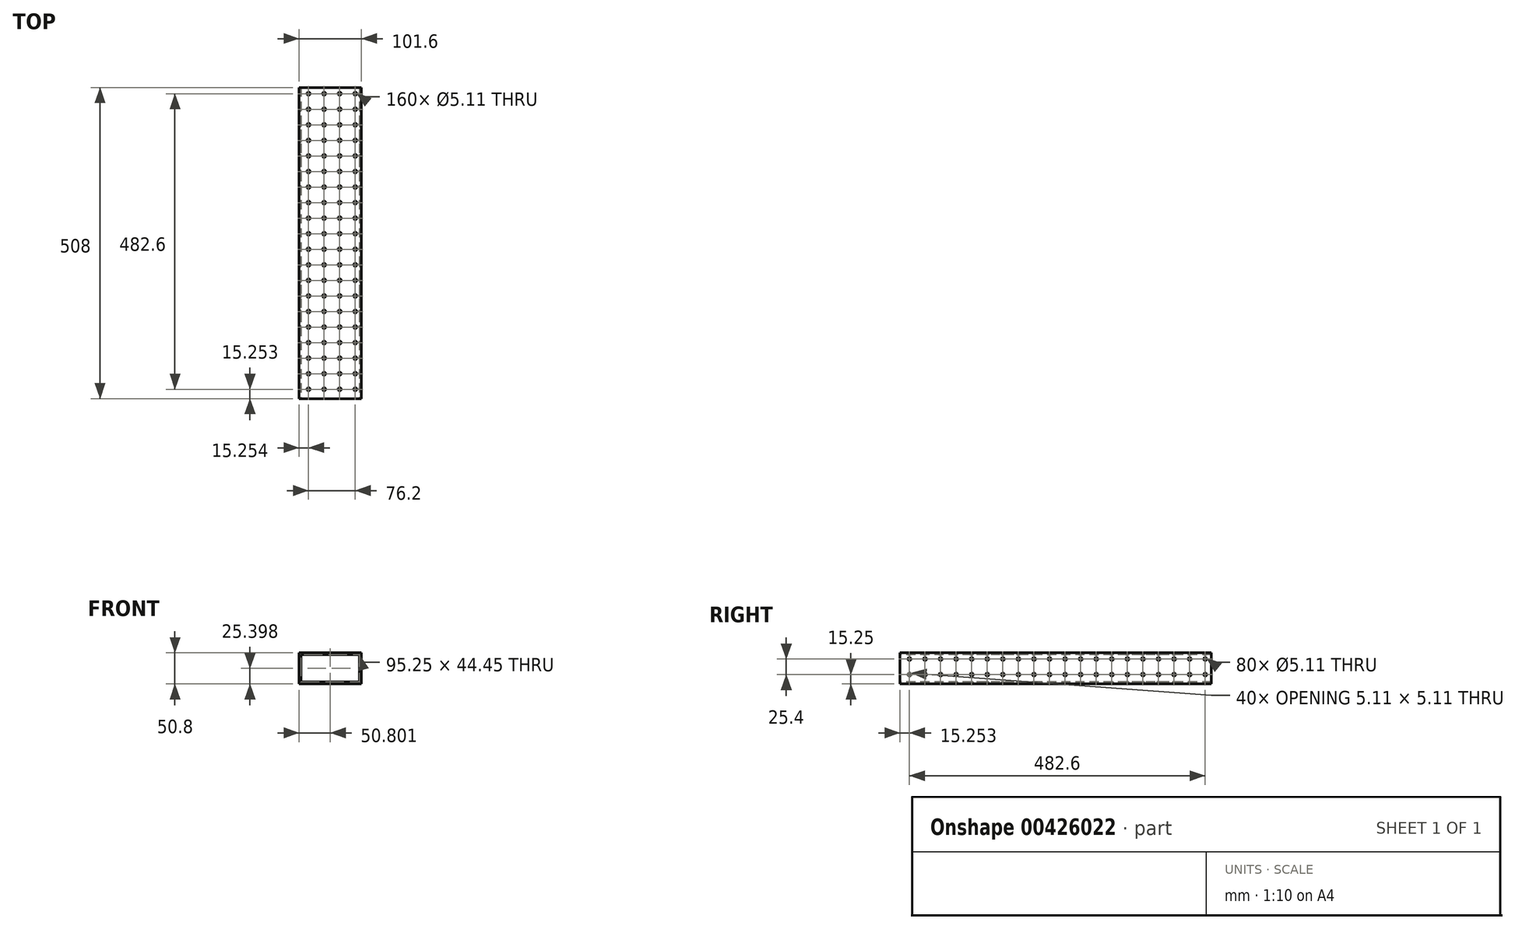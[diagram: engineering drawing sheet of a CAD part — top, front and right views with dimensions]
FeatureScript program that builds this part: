
annotation { "Feature Type Name" : "Feature", "Feature Type Description" : "" }
export const myFeature = defineFeature(function(context is Context, id is Id, definition is map)
    precondition{}
    {
        {
            var Q0;
            Q0=qCreatedBy(makeId("Front.planeOp"),FACE);
            var sketch = newSketch(context, id + "F0", { "sketchPlane" : qUnion([Q0])});
            skLineSegment(sketch, "E0.bottom", {"start": v(-35.52, 28.35) * mm, "end": v(66.08, 28.35) * mm});
            skLineSegment(sketch, "E0.top", {"start": v(-35.52, -22.45) * mm, "end": v(66.08, -22.45) * mm});
            skLineSegment(sketch, "E0.left", {"start": v(-35.52, 28.35) * mm, "end": v(-35.52, -22.45) * mm});
            skLineSegment(sketch, "E0.right", {"start": v(66.08, 28.35) * mm, "end": v(66.08, -22.45) * mm});
            skSolve(sketch);
        }
        {
            var Q0;
            Q0=makeQuery(id+"F0.imprint","IMPRINT",FACE,{"disambiguationData":[TD([[makeQuery(id+"F0.imprint","IMPRINT",EDGE,{"derivedFrom":sQuery(id+"F0.wireOp",EDGE,"E0.bottom")}),-1.0]])]});
            extrude(context, id + "F1", {"entities" : qUnion([Q0]), "depth" : 508 * mm});
        }
        {
            var Q0;
            Q0=makeQuery(id+"F1.opExtrude","CAP_FACE",FACE,{"disambiguationData":[OSD([sQuery(id+"F0.wireOp",EDGE,"E0.bottom"),sQuery(id+"F0.wireOp",EDGE,"E0.top"),sQuery(id+"F0.wireOp",EDGE,"E0.left"),sQuery(id+"F0.wireOp",EDGE,"E0.right")])],"isStart":false});
            var sketch = newSketch(context, id + "F2", { "sketchPlane" : qUnion([Q0])});
            skLineSegment(sketch, "E1.bottom", {"start": v(-32.34, 25.17) * mm, "end": v(62.9, 25.17) * mm});
            skLineSegment(sketch, "E1.top", {"start": v(-32.34, -19.28) * mm, "end": v(62.9, -19.28) * mm});
            skLineSegment(sketch, "E1.left", {"start": v(-32.34, 25.17) * mm, "end": v(-32.34, -19.28) * mm});
            skLineSegment(sketch, "E1.right", {"start": v(62.9, 25.17) * mm, "end": v(62.9, -19.28) * mm});
            skSolve(sketch);
        }
        {
            var Q0;
            Q0=makeQuery(id+"F2.imprint","IMPRINT",FACE,{"disambiguationData":[TD([[makeQuery(id+"F2.imprint","IMPRINT",EDGE,{"derivedFrom":sQuery(id+"F2.wireOp",EDGE,"E1.bottom")}),-1.0]])]});
            extrude(context, id + "F3", {"entities" : qUnion([Q0]), "operationType" : NewBodyOperationType.REMOVE, "oppositeDirection" : true, "depth" : 533.4 * mm});
        }
        {
            var Q0;
            Q0=makeQuery(id+"F1.opExtrude","SWEPT_FACE",FACE,{"disambiguationData":[OSD([sQuery(id+"F0.wireOp",EDGE,"E0.top")])]});
            var sketch = newSketch(context, id + "F4", { "sketchPlane" : qUnion([Q0])});
            skCircle(sketch, "E2", {"center": v(-20.27, 492.75) * mm, "radius": 2.55 * mm});
            skCircle(sketch, "E3.0.1.0", {"center": v(-20.27, 467.35) * mm, "radius": 2.55 * mm});
            skCircle(sketch, "E3.0.2.0", {"center": v(-20.27, 441.95) * mm, "radius": 2.55 * mm});
            skCircle(sketch, "E3.0.3.0", {"center": v(-20.27, 416.55) * mm, "radius": 2.55 * mm});
            skCircle(sketch, "E3.0.4.0", {"center": v(-20.27, 391.15) * mm, "radius": 2.55 * mm});
            skCircle(sketch, "E3.0.5.0", {"center": v(-20.27, 365.75) * mm, "radius": 2.55 * mm});
            skCircle(sketch, "E3.0.6.0", {"center": v(-20.27, 340.35) * mm, "radius": 2.55 * mm});
            skCircle(sketch, "E3.0.7.0", {"center": v(-20.27, 314.95) * mm, "radius": 2.55 * mm});
            skCircle(sketch, "E3.0.8.0", {"center": v(-20.27, 289.55) * mm, "radius": 2.55 * mm});
            skCircle(sketch, "E3.0.9.0", {"center": v(-20.27, 264.15) * mm, "radius": 2.55 * mm});
            skCircle(sketch, "E3.0.10.0", {"center": v(-20.27, 238.75) * mm, "radius": 2.55 * mm});
            skCircle(sketch, "E3.0.11.0", {"center": v(-20.27, 213.35) * mm, "radius": 2.55 * mm});
            skCircle(sketch, "E3.0.12.0", {"center": v(-20.27, 187.95) * mm, "radius": 2.55 * mm});
            skCircle(sketch, "E3.0.13.0", {"center": v(-20.27, 162.55) * mm, "radius": 2.55 * mm});
            skCircle(sketch, "E3.0.14.0", {"center": v(-20.27, 137.15) * mm, "radius": 2.55 * mm});
            skCircle(sketch, "E3.0.15.0", {"center": v(-20.27, 111.75) * mm, "radius": 2.55 * mm});
            skCircle(sketch, "E3.0.16.0", {"center": v(-20.27, 86.35) * mm, "radius": 2.55 * mm});
            skCircle(sketch, "E3.0.17.0", {"center": v(-20.27, 60.95) * mm, "radius": 2.55 * mm});
            skCircle(sketch, "E3.0.18.0", {"center": v(-20.27, 35.55) * mm, "radius": 2.55 * mm});
            skCircle(sketch, "E3.0.19.0", {"center": v(-20.27, 10.15) * mm, "radius": 2.55 * mm});
            skCircle(sketch, "E3.1.0.0", {"center": v(5.13, 492.75) * mm, "radius": 2.55 * mm});
            skCircle(sketch, "E3.1.1.0", {"center": v(5.13, 467.35) * mm, "radius": 2.55 * mm});
            skCircle(sketch, "E3.1.2.0", {"center": v(5.13, 441.95) * mm, "radius": 2.55 * mm});
            skCircle(sketch, "E3.1.3.0", {"center": v(5.13, 416.55) * mm, "radius": 2.55 * mm});
            skCircle(sketch, "E3.1.4.0", {"center": v(5.13, 391.15) * mm, "radius": 2.55 * mm});
            skCircle(sketch, "E3.1.5.0", {"center": v(5.13, 365.75) * mm, "radius": 2.55 * mm});
            skCircle(sketch, "E3.1.6.0", {"center": v(5.13, 340.35) * mm, "radius": 2.55 * mm});
            skCircle(sketch, "E3.1.7.0", {"center": v(5.13, 314.95) * mm, "radius": 2.55 * mm});
            skCircle(sketch, "E3.1.8.0", {"center": v(5.13, 289.55) * mm, "radius": 2.55 * mm});
            skCircle(sketch, "E3.1.9.0", {"center": v(5.13, 264.15) * mm, "radius": 2.55 * mm});
            skCircle(sketch, "E3.1.10.0", {"center": v(5.13, 238.75) * mm, "radius": 2.55 * mm});
            skCircle(sketch, "E3.1.11.0", {"center": v(5.13, 213.35) * mm, "radius": 2.55 * mm});
            skCircle(sketch, "E3.1.12.0", {"center": v(5.13, 187.95) * mm, "radius": 2.55 * mm});
            skCircle(sketch, "E3.1.13.0", {"center": v(5.13, 162.55) * mm, "radius": 2.55 * mm});
            skCircle(sketch, "E3.1.14.0", {"center": v(5.13, 137.15) * mm, "radius": 2.55 * mm});
            skCircle(sketch, "E3.1.15.0", {"center": v(5.13, 111.75) * mm, "radius": 2.55 * mm});
            skCircle(sketch, "E3.1.16.0", {"center": v(5.13, 86.35) * mm, "radius": 2.55 * mm});
            skCircle(sketch, "E3.1.17.0", {"center": v(5.13, 60.95) * mm, "radius": 2.55 * mm});
            skCircle(sketch, "E3.1.18.0", {"center": v(5.13, 35.55) * mm, "radius": 2.55 * mm});
            skCircle(sketch, "E3.1.19.0", {"center": v(5.13, 10.15) * mm, "radius": 2.55 * mm});
            skCircle(sketch, "E3.2.0.0", {"center": v(30.53, 492.75) * mm, "radius": 2.55 * mm});
            skCircle(sketch, "E3.2.1.0", {"center": v(30.53, 467.35) * mm, "radius": 2.55 * mm});
            skCircle(sketch, "E3.2.2.0", {"center": v(30.53, 441.95) * mm, "radius": 2.55 * mm});
            skCircle(sketch, "E3.2.3.0", {"center": v(30.53, 416.55) * mm, "radius": 2.55 * mm});
            skCircle(sketch, "E3.2.4.0", {"center": v(30.53, 391.15) * mm, "radius": 2.55 * mm});
            skCircle(sketch, "E3.2.5.0", {"center": v(30.53, 365.75) * mm, "radius": 2.55 * mm});
            skCircle(sketch, "E3.2.6.0", {"center": v(30.53, 340.35) * mm, "radius": 2.55 * mm});
            skCircle(sketch, "E3.2.7.0", {"center": v(30.53, 314.95) * mm, "radius": 2.55 * mm});
            skCircle(sketch, "E3.2.8.0", {"center": v(30.53, 289.55) * mm, "radius": 2.55 * mm});
            skCircle(sketch, "E3.2.9.0", {"center": v(30.53, 264.15) * mm, "radius": 2.55 * mm});
            skCircle(sketch, "E3.2.10.0", {"center": v(30.53, 238.75) * mm, "radius": 2.55 * mm});
            skCircle(sketch, "E3.2.11.0", {"center": v(30.53, 213.35) * mm, "radius": 2.55 * mm});
            skCircle(sketch, "E3.2.12.0", {"center": v(30.53, 187.95) * mm, "radius": 2.55 * mm});
            skCircle(sketch, "E3.2.13.0", {"center": v(30.53, 162.55) * mm, "radius": 2.55 * mm});
            skCircle(sketch, "E3.2.14.0", {"center": v(30.53, 137.15) * mm, "radius": 2.55 * mm});
            skCircle(sketch, "E3.2.15.0", {"center": v(30.53, 111.75) * mm, "radius": 2.55 * mm});
            skCircle(sketch, "E3.2.16.0", {"center": v(30.53, 86.35) * mm, "radius": 2.55 * mm});
            skCircle(sketch, "E3.2.17.0", {"center": v(30.53, 60.95) * mm, "radius": 2.55 * mm});
            skCircle(sketch, "E3.2.18.0", {"center": v(30.53, 35.55) * mm, "radius": 2.55 * mm});
            skCircle(sketch, "E3.2.19.0", {"center": v(30.53, 10.15) * mm, "radius": 2.55 * mm});
            skCircle(sketch, "E3.3.0.0", {"center": v(55.93, 492.75) * mm, "radius": 2.55 * mm});
            skCircle(sketch, "E3.3.1.0", {"center": v(55.93, 467.35) * mm, "radius": 2.55 * mm});
            skCircle(sketch, "E3.3.2.0", {"center": v(55.93, 441.95) * mm, "radius": 2.55 * mm});
            skCircle(sketch, "E3.3.3.0", {"center": v(55.93, 416.55) * mm, "radius": 2.55 * mm});
            skCircle(sketch, "E3.3.4.0", {"center": v(55.93, 391.15) * mm, "radius": 2.55 * mm});
            skCircle(sketch, "E3.3.5.0", {"center": v(55.93, 365.75) * mm, "radius": 2.55 * mm});
            skCircle(sketch, "E3.3.6.0", {"center": v(55.93, 340.35) * mm, "radius": 2.55 * mm});
            skCircle(sketch, "E3.3.7.0", {"center": v(55.93, 314.95) * mm, "radius": 2.55 * mm});
            skCircle(sketch, "E3.3.8.0", {"center": v(55.93, 289.55) * mm, "radius": 2.55 * mm});
            skCircle(sketch, "E3.3.9.0", {"center": v(55.93, 264.15) * mm, "radius": 2.55 * mm});
            skCircle(sketch, "E3.3.10.0", {"center": v(55.93, 238.75) * mm, "radius": 2.55 * mm});
            skCircle(sketch, "E3.3.11.0", {"center": v(55.93, 213.35) * mm, "radius": 2.55 * mm});
            skCircle(sketch, "E3.3.12.0", {"center": v(55.93, 187.95) * mm, "radius": 2.55 * mm});
            skCircle(sketch, "E3.3.13.0", {"center": v(55.93, 162.55) * mm, "radius": 2.55 * mm});
            skCircle(sketch, "E3.3.14.0", {"center": v(55.93, 137.15) * mm, "radius": 2.55 * mm});
            skCircle(sketch, "E3.3.15.0", {"center": v(55.93, 111.75) * mm, "radius": 2.55 * mm});
            skCircle(sketch, "E3.3.16.0", {"center": v(55.93, 86.35) * mm, "radius": 2.55 * mm});
            skCircle(sketch, "E3.3.17.0", {"center": v(55.93, 60.95) * mm, "radius": 2.55 * mm});
            skCircle(sketch, "E3.3.18.0", {"center": v(55.93, 35.55) * mm, "radius": 2.55 * mm});
            skCircle(sketch, "E3.3.19.0", {"center": v(55.93, 10.15) * mm, "radius": 2.55 * mm});
            skLineSegment(sketch, "E3.direction1", {"start": v(-20.27, 492.75) * mm, "end": v(5.13, 492.75) * mm, "construction": true});
            skLineSegment(sketch, "E3.direction2", {"start": v(-20.27, 492.75) * mm, "end": v(-20.27, 467.35) * mm, "construction": true});
            skSolve(sketch);
        }
        {
            var Q0;
            Q0 = qSketchRegion(id + "F4", true);
            extrude(context, id + "F5", {"entities" : qUnion([Q0]), "operationType" : NewBodyOperationType.REMOVE, "oppositeDirection" : true, "depth" : 508 * mm});
        }
        {
            var Q0;
            Q0=makeQuery(id+"F1.opExtrude","SWEPT_FACE",FACE,{"disambiguationData":[OSD([sQuery(id+"F0.wireOp",EDGE,"E0.right")])]});
            var sketch = newSketch(context, id + "F6", { "sketchPlane" : qUnion([Q0])});
            skCircle(sketch, "E4", {"center": v(-492.75, -7.2) * mm, "radius": 2.55 * mm});
            skCircle(sketch, "E5.0.1.0", {"center": v(-492.75, 18.2) * mm, "radius": 2.55 * mm});
            skCircle(sketch, "E5.1.0.0", {"center": v(-467.35, -7.2) * mm, "radius": 2.55 * mm});
            skCircle(sketch, "E5.1.1.0", {"center": v(-467.35, 18.2) * mm, "radius": 2.55 * mm});
            skCircle(sketch, "E5.2.0.0", {"center": v(-441.95, -7.2) * mm, "radius": 2.55 * mm});
            skCircle(sketch, "E5.2.1.0", {"center": v(-441.95, 18.2) * mm, "radius": 2.55 * mm});
            skCircle(sketch, "E5.3.0.0", {"center": v(-416.55, -7.2) * mm, "radius": 2.55 * mm});
            skCircle(sketch, "E5.3.1.0", {"center": v(-416.55, 18.2) * mm, "radius": 2.55 * mm});
            skCircle(sketch, "E5.4.0.0", {"center": v(-391.15, -7.2) * mm, "radius": 2.55 * mm});
            skCircle(sketch, "E5.4.1.0", {"center": v(-391.15, 18.2) * mm, "radius": 2.55 * mm});
            skCircle(sketch, "E5.5.0.0", {"center": v(-365.75, -7.2) * mm, "radius": 2.55 * mm});
            skCircle(sketch, "E5.5.1.0", {"center": v(-365.75, 18.2) * mm, "radius": 2.55 * mm});
            skCircle(sketch, "E5.6.0.0", {"center": v(-340.35, -7.2) * mm, "radius": 2.55 * mm});
            skCircle(sketch, "E5.6.1.0", {"center": v(-340.35, 18.2) * mm, "radius": 2.55 * mm});
            skCircle(sketch, "E5.7.0.0", {"center": v(-314.95, -7.2) * mm, "radius": 2.55 * mm});
            skCircle(sketch, "E5.7.1.0", {"center": v(-314.95, 18.2) * mm, "radius": 2.55 * mm});
            skCircle(sketch, "E5.8.0.0", {"center": v(-289.55, -7.2) * mm, "radius": 2.55 * mm});
            skCircle(sketch, "E5.8.1.0", {"center": v(-289.55, 18.2) * mm, "radius": 2.55 * mm});
            skCircle(sketch, "E5.9.0.0", {"center": v(-264.15, -7.2) * mm, "radius": 2.55 * mm});
            skCircle(sketch, "E5.9.1.0", {"center": v(-264.15, 18.2) * mm, "radius": 2.55 * mm});
            skCircle(sketch, "E5.10.0.0", {"center": v(-238.75, -7.2) * mm, "radius": 2.55 * mm});
            skCircle(sketch, "E5.10.1.0", {"center": v(-238.75, 18.2) * mm, "radius": 2.55 * mm});
            skCircle(sketch, "E5.11.0.0", {"center": v(-213.35, -7.2) * mm, "radius": 2.55 * mm});
            skCircle(sketch, "E5.11.1.0", {"center": v(-213.35, 18.2) * mm, "radius": 2.55 * mm});
            skCircle(sketch, "E5.12.0.0", {"center": v(-187.95, -7.2) * mm, "radius": 2.55 * mm});
            skCircle(sketch, "E5.12.1.0", {"center": v(-187.95, 18.2) * mm, "radius": 2.55 * mm});
            skCircle(sketch, "E5.13.0.0", {"center": v(-162.55, -7.2) * mm, "radius": 2.55 * mm});
            skCircle(sketch, "E5.13.1.0", {"center": v(-162.55, 18.2) * mm, "radius": 2.55 * mm});
            skCircle(sketch, "E5.14.0.0", {"center": v(-137.15, -7.2) * mm, "radius": 2.55 * mm});
            skCircle(sketch, "E5.14.1.0", {"center": v(-137.15, 18.2) * mm, "radius": 2.55 * mm});
            skCircle(sketch, "E5.15.0.0", {"center": v(-111.75, -7.2) * mm, "radius": 2.55 * mm});
            skCircle(sketch, "E5.15.1.0", {"center": v(-111.75, 18.2) * mm, "radius": 2.55 * mm});
            skCircle(sketch, "E5.16.0.0", {"center": v(-86.35, -7.2) * mm, "radius": 2.55 * mm});
            skCircle(sketch, "E5.16.1.0", {"center": v(-86.35, 18.2) * mm, "radius": 2.55 * mm});
            skCircle(sketch, "E5.17.0.0", {"center": v(-60.95, -7.2) * mm, "radius": 2.55 * mm});
            skCircle(sketch, "E5.17.1.0", {"center": v(-60.95, 18.2) * mm, "radius": 2.55 * mm});
            skCircle(sketch, "E5.18.0.0", {"center": v(-35.55, -7.2) * mm, "radius": 2.55 * mm});
            skCircle(sketch, "E5.18.1.0", {"center": v(-35.55, 18.2) * mm, "radius": 2.55 * mm});
            skCircle(sketch, "E5.19.0.0", {"center": v(-10.15, -7.2) * mm, "radius": 2.55 * mm});
            skCircle(sketch, "E5.19.1.0", {"center": v(-10.15, 18.2) * mm, "radius": 2.55 * mm});
            skLineSegment(sketch, "E5.direction1", {"start": v(-492.75, -7.2) * mm, "end": v(-467.35, -7.2) * mm, "construction": true});
            skLineSegment(sketch, "E5.direction2", {"start": v(-492.75, -7.2) * mm, "end": v(-492.75, 18.2) * mm, "construction": true});
            skSolve(sketch);
        }
        {
            var Q0;
            Q0 = qSketchRegion(id + "F6", true);
            extrude(context, id + "F7", {"entities" : qUnion([Q0]), "operationType" : NewBodyOperationType.REMOVE, "oppositeDirection" : true, "depth" : 127 * mm});
        }
    });
